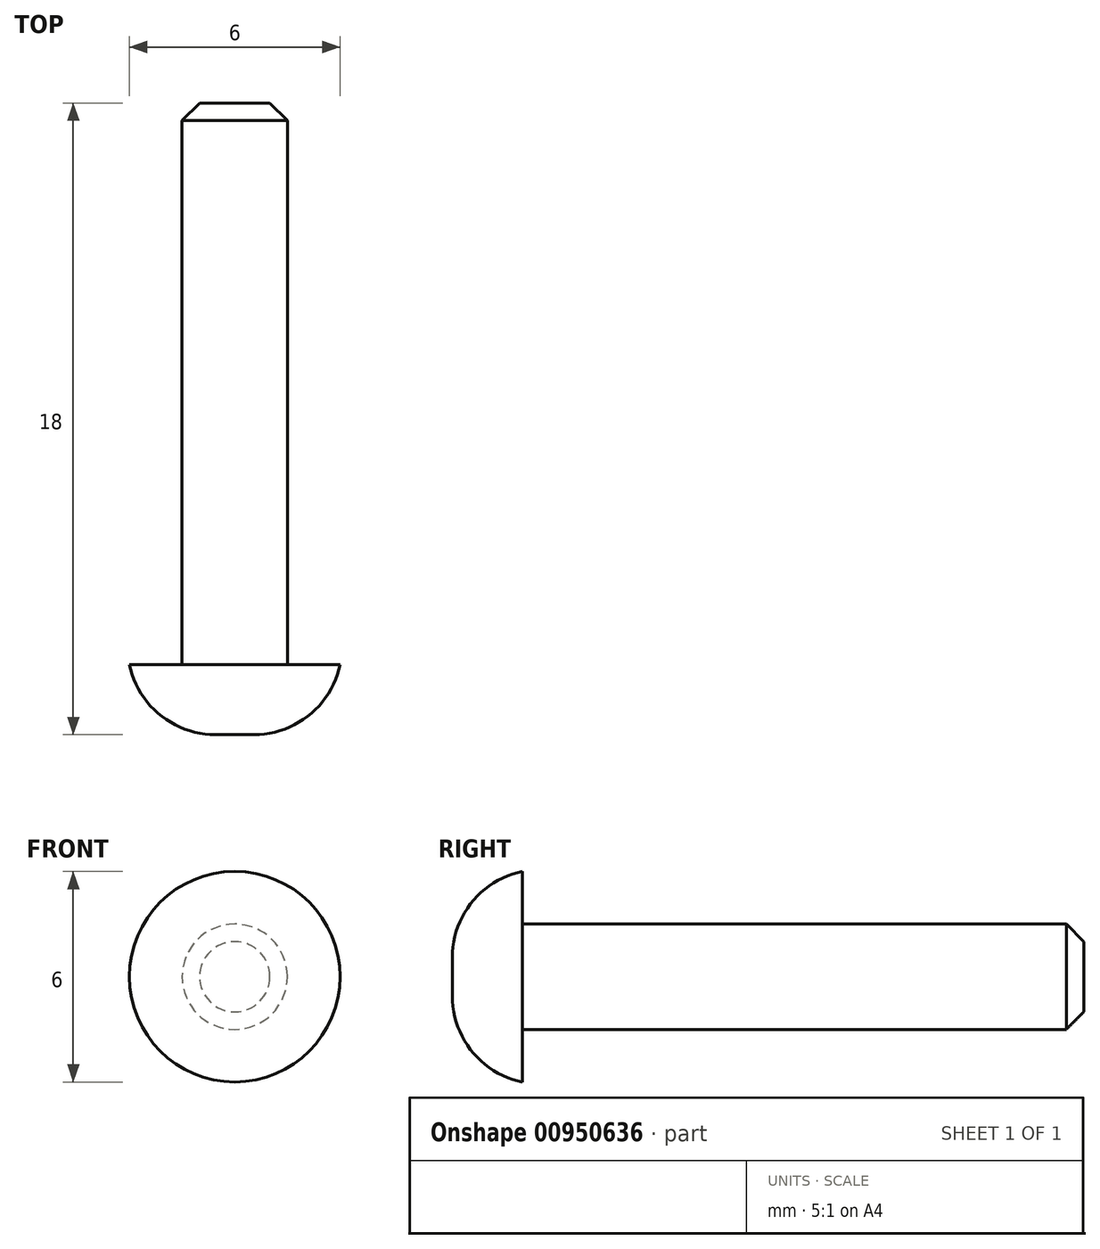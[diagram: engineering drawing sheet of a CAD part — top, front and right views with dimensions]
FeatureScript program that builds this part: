
annotation { "Feature Type Name" : "Feature", "Feature Type Description" : "" }
export const myFeature = defineFeature(function(context is Context, id is Id, definition is map)
    precondition{}
    {
        {
            var Q0;
            Q0=qCreatedBy(makeId("Front.planeOp"),FACE);
            var sketch = newSketch(context, id + "F0", { "sketchPlane" : qUnion([Q0])});
            skCircle(sketch, "E0", {"center": v(0, 0) * mm, "radius": 1.5 * mm});
            skCircle(sketch, "E1", {"center": v(0, 0) * mm, "radius": 3 * mm});
            skSolve(sketch);
        }
        {
            var Q0;
            Q0=makeQuery(id+"F0.imprint","IMPRINT",FACE,{"disambiguationData":[TD([[makeQuery(id+"F0.imprint","IMPRINT",EDGE,{"derivedFrom":sQuery(id+"F0.wireOp",EDGE,"E0")}),1.0]])]});
            extrude(context, id + "F1", {"entities" : qUnion([Q0]), "oppositeDirection" : true, "depth" : 16 * mm, "offsetDistance" : 25 * mm});
        }
        {
            var Q0;
            Q0=makeQuery(id+"F0.imprint","IMPRINT",FACE,{"disambiguationData":[TD([[makeQuery(id+"F0.imprint","IMPRINT",EDGE,{"derivedFrom":sQuery(id+"F0.wireOp",EDGE,"E0")}),-1.0]])]});
            var Q1;
            Q1=makeQuery(id+"F0.imprint","IMPRINT",FACE,{"disambiguationData":[TD([[makeQuery(id+"F0.imprint","IMPRINT",EDGE,{"derivedFrom":sQuery(id+"F0.wireOp",EDGE,"E0")}),1.0]])]});
            extrude(context, id + "F2", {"entities" : qUnion([Q0, Q1]), "operationType" : NewBodyOperationType.ADD, "depth" : 2 * mm, "offsetDistance" : 25 * mm});
        }
        {
            var Q0;
            Q0=makeQuery(id+"F2.opExtrude","CAP_EDGE",EDGE,{"disambiguationData":[OSD([sQuery(id+"F0.wireOp",EDGE,"E1")])],"isStart":false});
            fillet(context, id + "F3", {"entities" : qUnion([Q0]), "radius" : 2.5 * mm, "tangentPropagation" : true, "allowEdgeOverflow" : false});
        }
        {
            var Q0;
            Q0=makeQuery(id+"F1.opExtrude","CAP_EDGE",EDGE,{"disambiguationData":[OSD([sQuery(id+"F0.wireOp",EDGE,"E0")])],"isStart":false});
            chamfer(context, id + "F4", {"entities" : qUnion([Q0]), "width" : 0.5 * mm, "tangentPropagation" : true});
        }
    });
